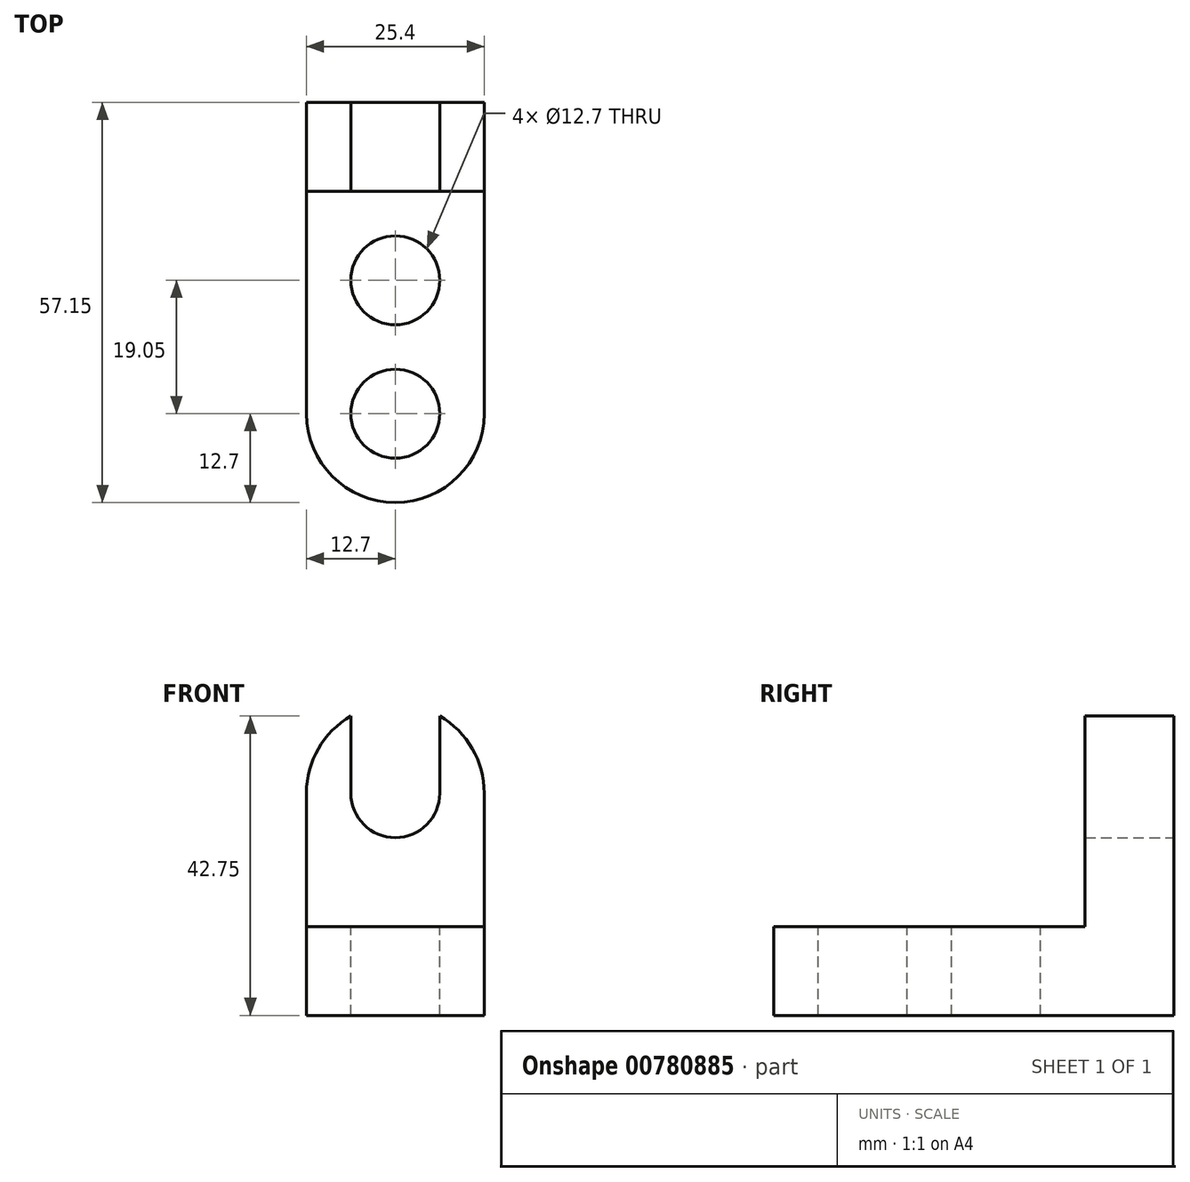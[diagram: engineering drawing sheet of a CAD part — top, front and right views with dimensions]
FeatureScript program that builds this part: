
annotation { "Feature Type Name" : "Feature", "Feature Type Description" : "" }
export const myFeature = defineFeature(function(context is Context, id is Id, definition is map)
    precondition{}
    {
        {
            var Q0;
            Q0=qCreatedBy(makeId("Right.planeOp"),FACE);
            var sketch = newSketch(context, id + "F0", { "sketchPlane" : qUnion([Q0])});
            skLineSegment(sketch, "E0", {"start": v(0, 0) * mm, "end": v(0, 44.45) * mm});
            skLineSegment(sketch, "E1", {"start": v(0, 44.45) * mm, "end": v(-12.7, 44.45) * mm});
            skLineSegment(sketch, "E2", {"start": v(-12.7, 44.45) * mm, "end": v(-12.7, 12.7) * mm});
            skLineSegment(sketch, "E3", {"start": v(-12.7, 12.7) * mm, "end": v(-57.15, 12.7) * mm});
            skLineSegment(sketch, "E4", {"start": v(-57.15, 12.7) * mm, "end": v(-57.15, 0) * mm});
            skLineSegment(sketch, "E5", {"start": v(-57.15, 0) * mm, "end": v(0, 0) * mm});
            skSolve(sketch);
        }
        {
            var Q0;
            Q0=makeQuery(id+"F0.imprint","IMPRINT",FACE,{"disambiguationData":[TD([[makeQuery(id+"F0.imprint","IMPRINT",EDGE,{"derivedFrom":sQuery(id+"F0.wireOp",EDGE,"E0")}),1.0]])]});
            extrude(context, id + "F1", {"entities" : qUnion([Q0]), "depth" : 25.4 * mm, "offsetDistance" : 25.4 * mm});
        }
        {
            var Q0;
            Q0=makeQuery(id+"F1.opExtrude","CAP_EDGE",EDGE,{"disambiguationData":[OSD([sQuery(id+"F0.wireOp",EDGE,"E1")])],"isStart":true});
            var Q1;
            Q1=makeQuery(id+"F1.opExtrude","CAP_EDGE",EDGE,{"disambiguationData":[OSD([sQuery(id+"F0.wireOp",EDGE,"E1")])],"isStart":false});
            fillet(context, id + "F2", {"entities" : qUnion([Q0, Q1]), "radius" : 12.7 * mm, "tangentPropagation" : true, "allowEdgeOverflow" : false});
        }
        {
            var Q0;
            Q0=makeQuery(id+"F1.opExtrude","CAP_EDGE",EDGE,{"disambiguationData":[OSD([sQuery(id+"F0.wireOp",EDGE,"E4")])],"isStart":false});
            var Q1;
            Q1=makeQuery(id+"F1.opExtrude","CAP_EDGE",EDGE,{"disambiguationData":[OSD([sQuery(id+"F0.wireOp",EDGE,"E4")])],"isStart":true});
            fillet(context, id + "F3", {"entities" : qUnion([Q0, Q1]), "radius" : 12.7 * mm, "tangentPropagation" : true, "allowEdgeOverflow" : false});
        }
        {
            var Q0;
            Q0=makeQuery(id+"F1.opExtrude","SWEPT_FACE",FACE,{"disambiguationData":[OSD([sQuery(id+"F0.wireOp",EDGE,"E3")])]});
            var sketch = newSketch(context, id + "F4", { "sketchPlane" : qUnion([Q0])});
            skCircle(sketch, "E6", {"center": v(12.7, -44.45) * mm, "radius": 6.35 * mm});
            skCircle(sketch, "E7", {"center": v(12.7, -25.4) * mm, "radius": 6.35 * mm});
            skPoint(sketch, "E7.centerSnap0", {"position": v(12.7, -57.15) * mm});
            skSolve(sketch);
        }
        {
            var Q0;
            Q0=makeQuery(id+"F1.opExtrude","SWEPT_FACE",FACE,{"disambiguationData":[OSD([sQuery(id+"F0.wireOp",EDGE,"E0")])]});
            var sketch = newSketch(context, id + "F5", { "sketchPlane" : qUnion([Q0])});
            skCircle(sketch, "E8", {"center": v(-12.7, 31.75) * mm, "radius": 6.35 * mm});
            skLineSegment(sketch, "E9", {"start": v(-19.05, 31.75) * mm, "end": v(-19.05, 42.75) * mm});
            skLineSegment(sketch, "E10", {"start": v(-6.35, 31.75) * mm, "end": v(-6.35, 42.75) * mm});
            skSolve(sketch);
        }
        {
            var Q0;
            Q0 = qSketchRegion(id + "F5", true);
            var Q1;
            {var subQ0=sQuery(id+"F5.wireOp",EDGE,"E9");Q1=makeQuery(id+"F5.imprint","IMPRINT",FACE,{"disambiguationData":[TD([[makeQuery(id+"F5.imprint","IMPRINT",EDGE,{"derivedFrom":subQ0}),-1.0]])]});}
            extrude(context, id + "F6", {"entities" : qUnion([Q0, Q1]), "operationType" : NewBodyOperationType.REMOVE, "oppositeDirection" : true, "depth" : 25.4 * mm, "offsetDistance" : 25.4 * mm});
        }
        {
            var Q0;
            Q0=makeQuery(id+"F4.imprint","IMPRINT",FACE,{"disambiguationData":[TD([[makeQuery(id+"F4.imprint","IMPRINT",EDGE,{"derivedFrom":sQuery(id+"F4.wireOp",EDGE,"E6")}),1.0]])]});
            var Q1;
            Q1=makeQuery(id+"F4.imprint","IMPRINT",FACE,{"disambiguationData":[TD([[makeQuery(id+"F4.imprint","IMPRINT",EDGE,{"derivedFrom":sQuery(id+"F4.wireOp",EDGE,"E7")}),1.0]])]});
            var Q2;
            Q2=sQuery(id+"F4.wireOp",EDGE,"E6");
            extrude(context, id + "F7", {"entities" : qUnion([Q0, Q1]), "operationType" : NewBodyOperationType.REMOVE, "surfaceEntities" : qUnion([Q2]), "oppositeDirection" : true, "depth" : 25.4 * mm, "offsetDistance" : 25.4 * mm});
        }
    });
